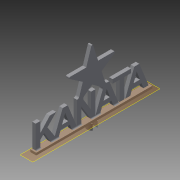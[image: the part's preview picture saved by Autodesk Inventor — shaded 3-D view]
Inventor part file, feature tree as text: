
AUTODESK INVENTOR PART (.ipt)
format: ipt  version: 2014 (Build 180170000, 170)  size: 253,440 bytes
history: native  units: mm
features: extrude x5, sketch x5, fillet x3, other x2, projected_geometry x2
ambient origin geometry x8: Origin, YZ Plane, XZ Plane, XY Plane, X Axis, Y Axis, Z Axis, Center Point
bodies: Body1 (feature_tree)
feature tree (17):
  other  "ソリッド1"
  extrude  "押し出し1"  TaperAngle=0.0deg  [1 undecoded]
  other  "作業平面1"
  extrude  "押し出し2"  TaperAngle=0.0deg  [1 undecoded]
  extrude  "押し出し3"  TaperAngle=0.0deg  [1 undecoded]
  extrude  "押し出し4"  TaperAngle=0.0deg  [1 undecoded]
  extrude  "押し出し5"  TaperAngle=0.0deg  [1 undecoded]
  fillet  "フィレット1"  [1 undecoded]
  fillet  "フィレット2"  Radius=3.0mm
  fillet  "フィレット3"  Radius=10.3mm
  sketch  "スケッチ1"
  sketch  "スケッチ2"
  sketch  "スケッチ3"
  sketch  "スケッチ5"
  projected_geometry  "投影ループ1"
  sketch  "スケッチ6"
  projected_geometry  "投影ループ2"
note: 6 required parameter values undecoded (feature->parameter linkage not recoverable at this tier; creation-order binding heuristic only, values carry confidence <= 0.55)
